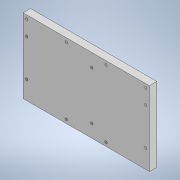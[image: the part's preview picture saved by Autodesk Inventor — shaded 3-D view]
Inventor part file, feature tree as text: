
AUTODESK INVENTOR PART (.ipt)
format: ipt  version: 2022.2 (Build 262287030, 287C)  size: 140,288 bytes
history: native  units: in
note: dims shown in document units (in); Inventor stores cm internally (conversion verified against a paired STEP export)
features: hole x3, sketch x3, extrude x1, projected_geometry x1
ambient origin geometry x8: Origin, YZ Plane, XZ Plane, XY Plane, X Axis, Y Axis, Z Axis, Center Point
bodies: Solid1 (feature_tree)
feature tree (8):
  extrude  "Extrusion1"  Depth=3.937in
  hole  "Hole1"  [1 undecoded]
  hole  "Hole2"  [1 undecoded]
  hole  "Hole3"  [1 undecoded]
  sketch  "Sketch1"  dims[d0=6.6929in d1=3.937in]
  projected_geometry  "Projected Loop1"
  sketch  "Sketch3"  dims[d2=0.3937in d3=0.0in d17=2.0997in]
  sketch  "Sketch4"  dims[d36=0.125in d37=0.2953in d38=0.1476in d39=0.0984in d40=90.0deg d41=0.1969in d42=0.0in d51=0.7874in d53=1.9685in d54=0.3937in d56=0.3937in d59=0.7874in d61=6.2992in d62=0.3937in d64=0.3937in d66=0.7874in d68=6.2992in d69=0.3937in d71=0.3937in d73=0.1969in d74=0.1969in d75=0.1969in d77=0.1969in d81=0.5906in d82=1.5748in d84=360.0deg d86=0.1181in d87=0.2953in d88=0.1476in d89=0.0984in d90=90.0deg d91=0.1969in d92=0.0in d94=1.2795in d95=0.7874in d97=2.5591in d98=0.3937in d100=0.3937in d102=0.1181in d103=0.315in d104=0.1476in d105=0.0984in d106=90.0deg d107=0.1969in d108=0.0in d109=3.6465in d110=0.7874in d112=2.0997in d113=0.7874in d115=3.5433in d118=0.9843in d4=0.3937in d5=0.3937in d6=0.3937in d7=0.0591in d8=0.0984in d9=0.1476in d10=0.5635in d11=0.2953in d12=0.8108in d13=0.0246in d14=0.2953in d15=0.1476in]
note: 3 required parameter values undecoded (feature->parameter linkage not recoverable at this tier; creation-order binding heuristic only, values carry confidence <= 0.55)
